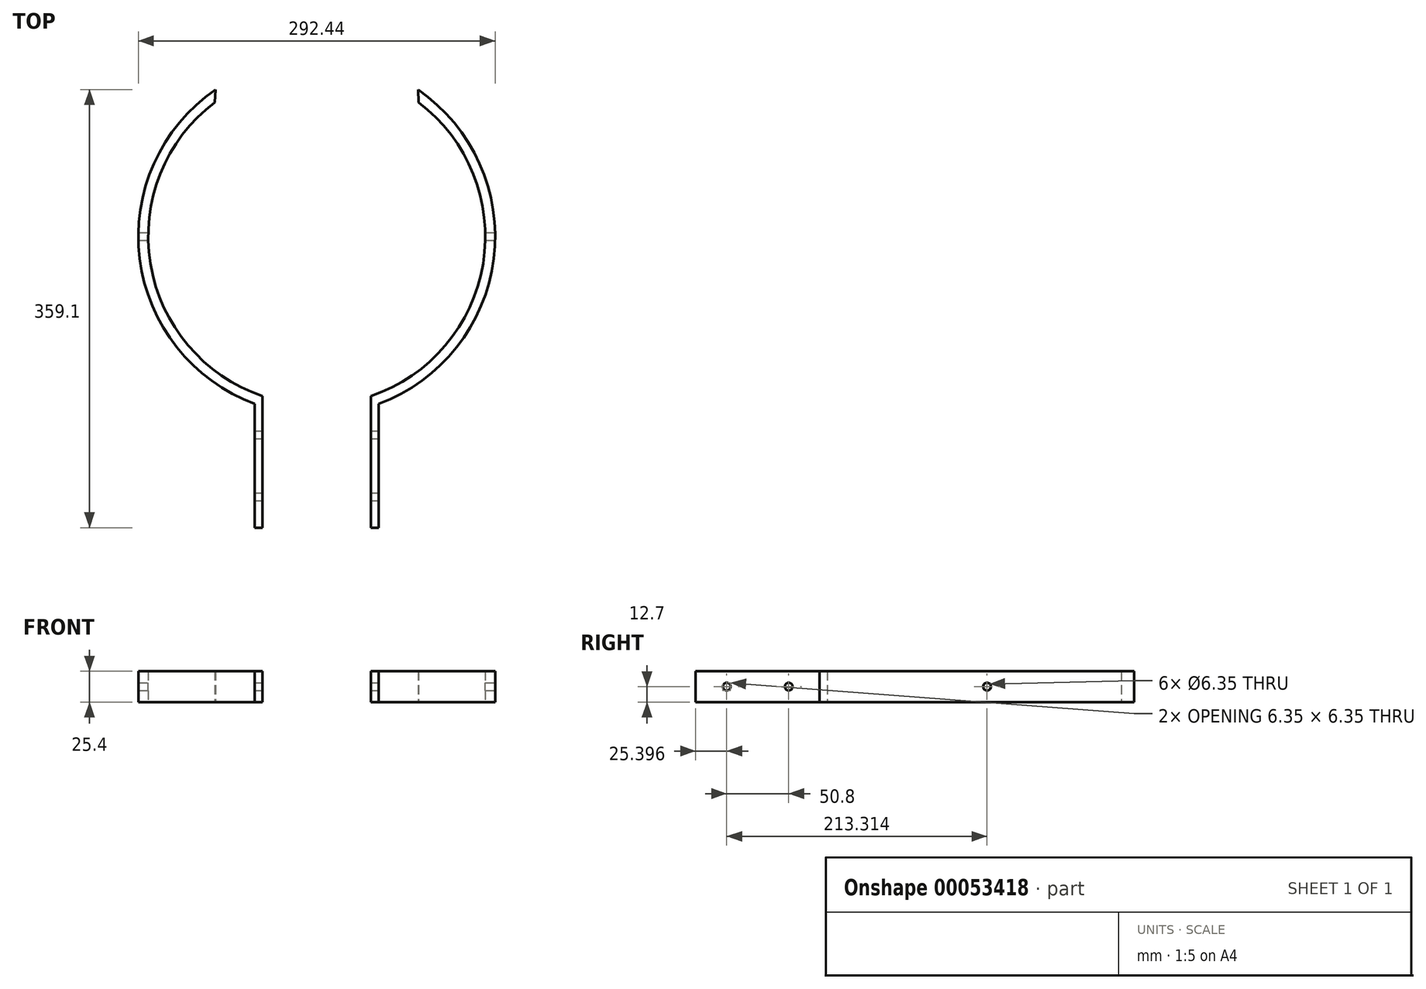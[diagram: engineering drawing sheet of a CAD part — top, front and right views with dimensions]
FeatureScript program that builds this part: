
annotation { "Feature Type Name" : "Feature", "Feature Type Description" : "" }
export const myFeature = defineFeature(function(context is Context, id is Id, definition is map)
    precondition{}
    {
        {
            var Q0;
            Q0=qCreatedBy(makeId("Top.planeOp"),FACE);
            var sketch = newSketch(context, id + "F0", { "sketchPlane" : qUnion([Q0])});
            skLineSegment(sketch, "E0", {"start": v(-44.45, -130.76) * mm, "end": v(-44.45, -238.71) * mm});
            skLineSegment(sketch, "E1", {"start": v(-44.45, -238.71) * mm, "end": v(-50.8, -238.71) * mm});
            skLineSegment(sketch, "E2", {"start": v(-50.8, -238.71) * mm, "end": v(-50.8, -137.11) * mm});
            skArc(sketch, "E3", {"start": v(-83.53, 110) * mm, "mid": v(-136.33, -22.13) * mm, "end": v(-44.45, -130.76) * mm});
            skArc(sketch, "E4", {"start": v(-82.98, 120.4) * mm, "mid": v(-145.1, -18.13) * mm, "end": v(-50.8, -137.11) * mm});
            skLineSegment(sketch, "E5", {"start": v(-82.98, 120.4) * mm, "end": v(-83.53, 110) * mm});
            skLineSegment(sketch, "E6.MirrorCS", {"start": v(82.98, 120.4) * mm, "end": v(83.53, 110) * mm});
            skLineSegment(sketch, "E7.MirrorCS", {"start": v(44.45, -238.71) * mm, "end": v(50.8, -238.71) * mm});
            skArc(sketch, "E8.MirrorCS", {"start": v(82.98, 120.4) * mm, "mid": v(145.1, -18.13) * mm, "end": v(50.8, -137.11) * mm});
            skLineSegment(sketch, "E9.MirrorCS", {"start": v(50.8, -238.71) * mm, "end": v(50.8, -137.11) * mm});
            skLineSegment(sketch, "E10.MirrorCS", {"start": v(44.45, -130.76) * mm, "end": v(44.45, -238.71) * mm});
            skArc(sketch, "E11.MirrorCS", {"start": v(83.53, 110) * mm, "mid": v(136.33, -22.13) * mm, "end": v(44.45, -130.76) * mm});
            skArc(sketch, "E12", {"start": v(137.78, -9.52) * mm, "mid": v(138.11, 0) * mm, "end": v(137.78, 9.53) * mm});
            skLineSegment(sketch, "E13", {"start": v(137.78, 9.53) * mm, "end": v(145.91, 9.53) * mm});
            skLineSegment(sketch, "E14", {"start": v(145.91, 9.53) * mm, "end": v(145.91, -9.52) * mm});
            skLineSegment(sketch, "E15", {"start": v(145.91, -9.52) * mm, "end": v(137.78, -9.52) * mm});
            skArc(sketch, "E16.MirrorCS", {"start": v(-137.78, -9.52) * mm, "mid": v(-138.11, 0) * mm, "end": v(-137.78, 9.53) * mm});
            skLineSegment(sketch, "E17.MirrorCS", {"start": v(-145.91, -9.52) * mm, "end": v(-137.78, -9.52) * mm});
            skLineSegment(sketch, "E18.MirrorCS", {"start": v(-137.78, 9.53) * mm, "end": v(-145.91, 9.53) * mm});
            skLineSegment(sketch, "E19.MirrorCS", {"start": v(-145.91, 9.53) * mm, "end": v(-145.91, -9.52) * mm});
            skSolve(sketch);
        }
        {
            var Q0;
            Q0 = qSketchRegion(id + "F0", true);
            extrude(context, id + "F1", {"entities" : qUnion([Q0]), "depth" : 25.4 * mm});
        }
        {
            var Q0;
            Q0=qCreatedBy(makeId("Right.planeOp"),FACE);
            var sketch = newSketch(context, id + "F2", { "sketchPlane" : qUnion([Q0])});
            skCircle(sketch, "E20", {"center": v(0, 12.7) * mm, "radius": 3.18 * mm});
            skCircle(sketch, "E21", {"center": v(-162.51, 12.7) * mm, "radius": 3.18 * mm});
            skCircle(sketch, "E22", {"center": v(-213.31, 12.7) * mm, "radius": 3.18 * mm});
            skSolve(sketch);
        }
        {
            var Q0;
            Q0 = qSketchRegion(id + "F2", true);
            extrude(context, id + "F3", {"entities" : qUnion([Q0]), "operationType" : NewBodyOperationType.REMOVE, "endBound" : BoundingType.SYMMETRIC, "oppositeDirection" : true, "depth" : 406.4 * mm});
        }
    });
